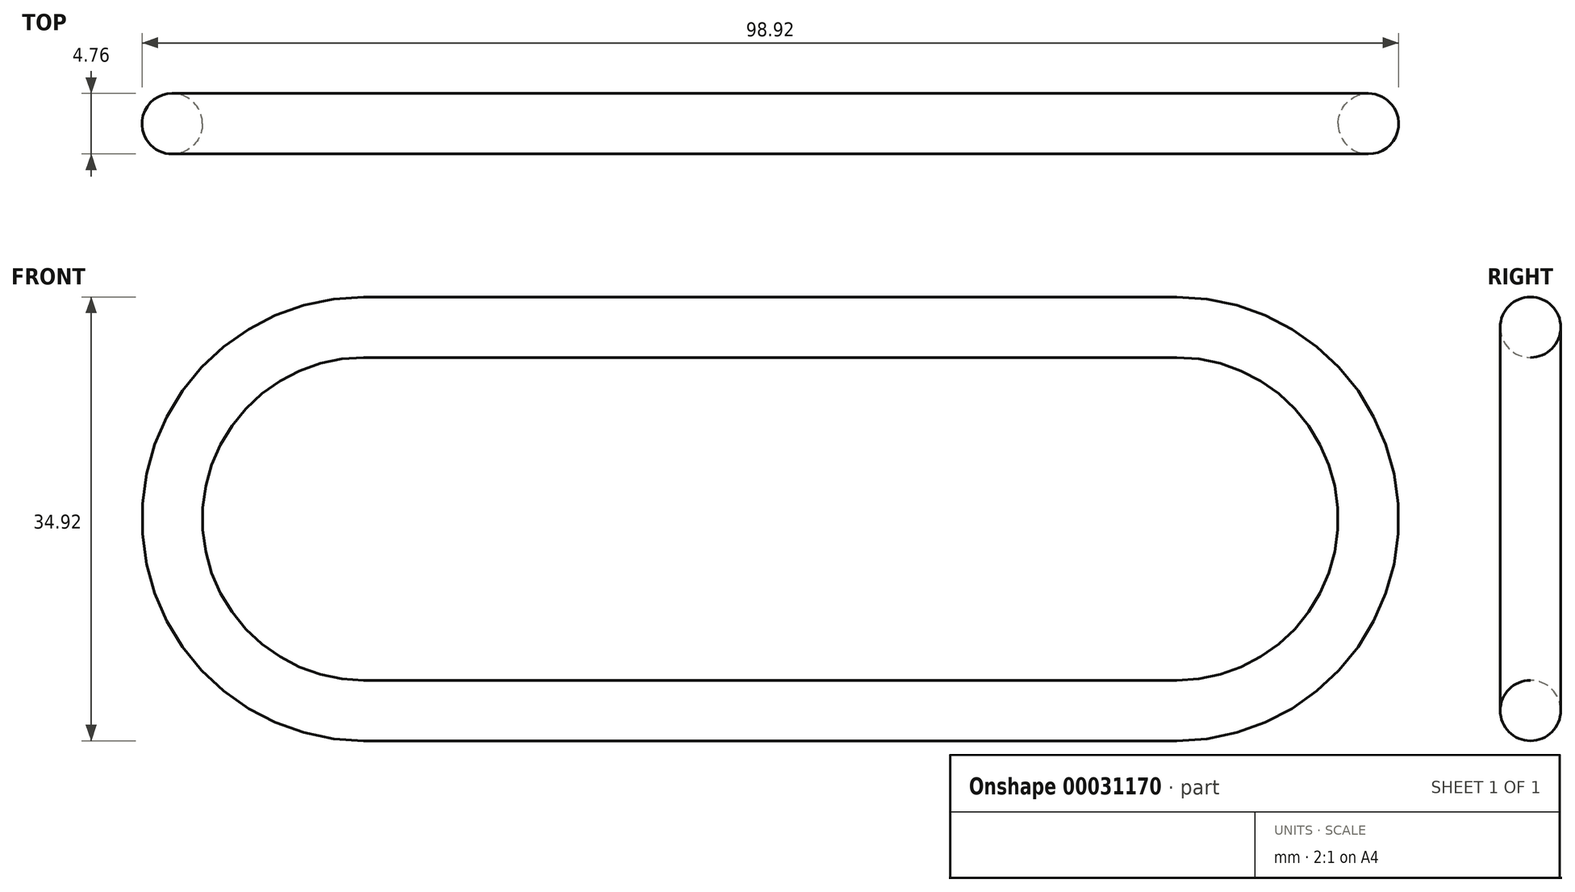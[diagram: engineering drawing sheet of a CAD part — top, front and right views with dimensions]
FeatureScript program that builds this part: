
annotation { "Feature Type Name" : "Feature", "Feature Type Description" : "" }
export const myFeature = defineFeature(function(context is Context, id is Id, definition is map)
    precondition{}
    {
        {
            var Q0;
            Q0=qCreatedBy(makeId("Front.planeOp"),FACE);
            var sketch = newSketch(context, id + "F0", { "sketchPlane" : qUnion([Q0])});
            skArc(sketch, "E0", {"start": v(0, 12.7) * mm, "mid": v(-12.7, 0) * mm, "end": v(0, -12.7) * mm});
            skArc(sketch, "E1", {"start": v(64, -12.7) * mm, "mid": v(76.7, 0) * mm, "end": v(64, 12.7) * mm});
            skLineSegment(sketch, "E2", {"start": v(0, 12.7) * mm, "end": v(64, 12.7) * mm});
            skLineSegment(sketch, "E3", {"start": v(0, -12.7) * mm, "end": v(64, -12.7) * mm});
            skLineSegment(sketch, "E4.0", {"start": v(0, 17.46) * mm, "end": v(64, 17.46) * mm});
            skArc(sketch, "E4.1", {"start": v(0, 17.46) * mm, "mid": v(-17.46, 0) * mm, "end": v(0, -17.46) * mm});
            skLineSegment(sketch, "E4.2", {"start": v(0, -17.46) * mm, "end": v(64, -17.46) * mm});
            skArc(sketch, "E4.3", {"start": v(64, -17.46) * mm, "mid": v(81.46, 0) * mm, "end": v(64, 17.46) * mm});
            skSolve(sketch);
        }
        {
            var Q0;
            Q0=qCreatedBy(makeId("Right.planeOp"),FACE);
            var sketch = newSketch(context, id + "F1", { "sketchPlane" : qUnion([Q0])});
            skCircle(sketch, "E5", {"center": v(0, 15.08) * mm, "radius": 2.38 * mm});
            skSolve(sketch);
        }
        {
            var Q0;
            Q0=makeQuery(id+"F1.imprint","IMPRINT",FACE,{"disambiguationData":[TD([[makeQuery(id+"F1.imprint","IMPRINT",EDGE,{"derivedFrom":sQuery(id+"F1.wireOp",EDGE,"E5")}),1.0]])]});
            var Q1;
            Q1=sQuery(id+"F0.wireOp",EDGE,"E2");
            var Q2;
            Q2=sQuery(id+"F0.wireOp",EDGE,"E1");
            var Q3;
            Q3=sQuery(id+"F0.wireOp",EDGE,"E3");
            var Q4;
            Q4=sQuery(id+"F0.wireOp",EDGE,"E0");
            sweep(context, id + "F2", {"profiles" : qUnion([Q0]), "path" : qUnion([Q1, Q2, Q3, Q4])});
        }
    });
